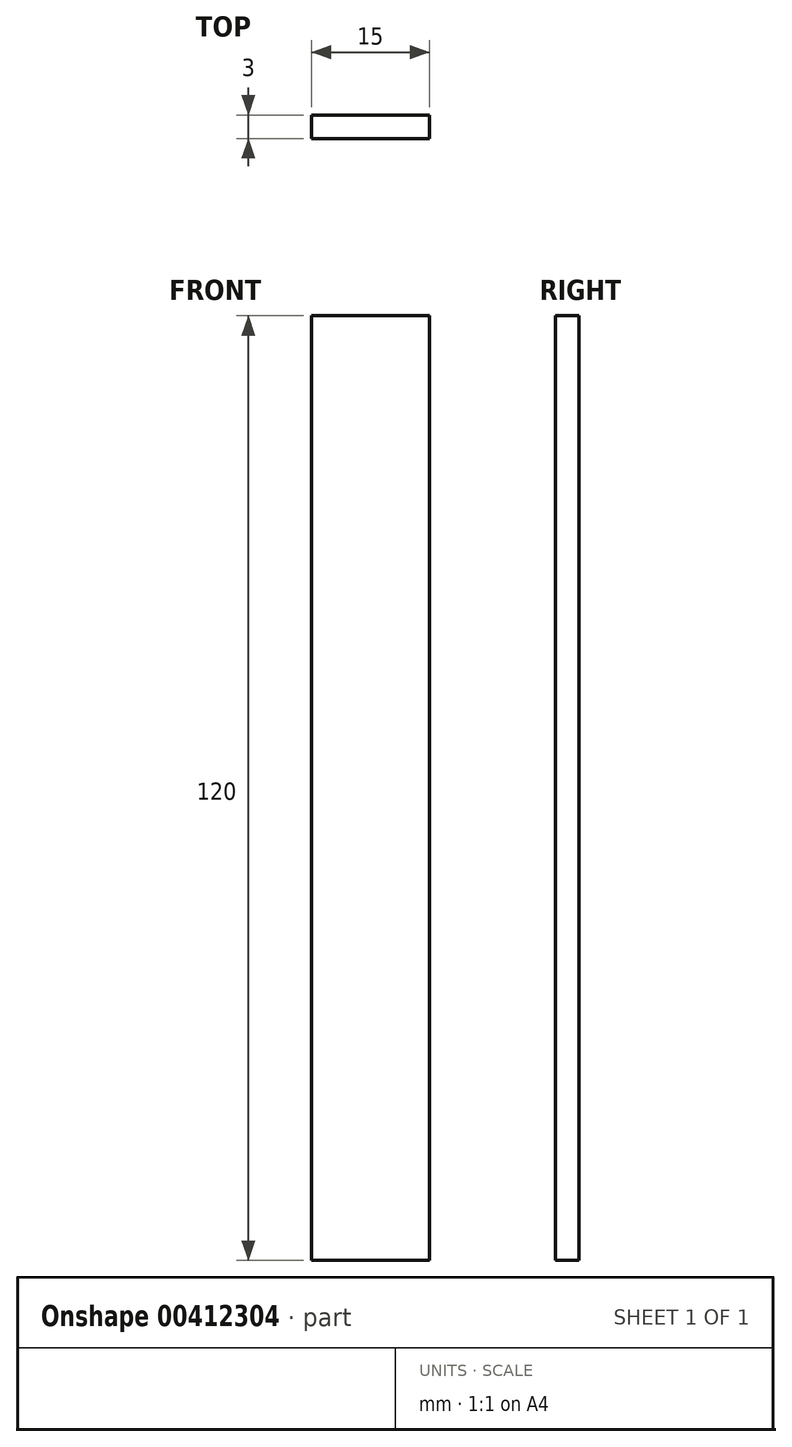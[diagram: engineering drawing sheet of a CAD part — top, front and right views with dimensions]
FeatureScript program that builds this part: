
annotation { "Feature Type Name" : "Feature", "Feature Type Description" : "" }
export const myFeature = defineFeature(function(context is Context, id is Id, definition is map)
    precondition{}
    {
        {
            var Q0;
            Q0=qCreatedBy(makeId("Front.planeOp"),FACE);
            var sketch = newSketch(context, id + "F0", { "sketchPlane" : qUnion([Q0])});
            skLineSegment(sketch, "E0.bottom", {"start": v(-8.84, 95.04) * mm, "end": v(6.16, 95.04) * mm});
            skLineSegment(sketch, "E0.top", {"start": v(-8.84, -24.96) * mm, "end": v(6.16, -24.96) * mm});
            skLineSegment(sketch, "E0.left", {"start": v(-8.84, 95.04) * mm, "end": v(-8.84, -24.96) * mm});
            skLineSegment(sketch, "E0.right", {"start": v(6.16, 95.04) * mm, "end": v(6.16, -24.96) * mm});
            skSolve(sketch);
        }
        {
            var Q0;
            Q0 = qSketchRegion(id + "F0", true);
            extrude(context, id + "F1", {"entities" : qUnion([Q0]), "depth" : 3 * mm});
        }
    });
